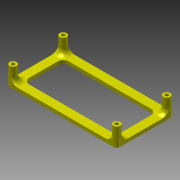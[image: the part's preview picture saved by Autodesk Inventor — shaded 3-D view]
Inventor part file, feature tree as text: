
AUTODESK INVENTOR PART (.ipt)
format: ipt  version: 2013 (Build 170138000, 138)  size: 189,952 bytes
history: native  units: mm
features: sketch x5, extrude x4, fillet x2, hole x1, projected_geometry x1
ambient origin geometry x8: Origin, YZ Plane, XZ Plane, XY Plane, X Axis, Y Axis, Z Axis, Center Point
bodies: Solid1 (feature_tree)
feature tree (13):
  extrude  "Extrusion1"  Depth=101.6mm
  hole  "Hole1"  [1 undecoded]
  extrude  "Extrusion2"  Depth=6.0mm
  extrude  "Extrusion3"  Depth=3.0mm TaperAngle=0.0deg
  extrude  "Extrusion4"  Depth=7.5mm
  fillet  "Fillet1"  Radius=7.5mm
  fillet  "Fillet2"  Radius=3.0mm
  sketch  "Sketch1"  dims[d0=50.8mm d2=101.6mm]
  sketch  "Sketch2"  dims[d3=16.0mm d4=0.0mm d5=43.815mm]
  sketch  "Sketch3"  dims[d7=90.678mm]
  sketch  "Sketch4"  dims[d8=3.0mm d9=6.0mm d10=6.5mm d11=3.0mm d12=90.0deg d13=8.0mm d14=20.594885mm d15=6.0mm]
  sketch  "Sketch5"  dims[d17=10.0mm d18=0.0mm d19=3.0mm d20=0.0mm d21=7.5mm d22=7.5mm d23=3.0mm d24=0.0mm d25=5.0mm d26=5.0mm]
  projected_geometry  "Project Cut Edges1"
note: 1 required parameter value undecoded (feature->parameter linkage not recoverable at this tier; creation-order binding heuristic only, values carry confidence <= 0.55)
